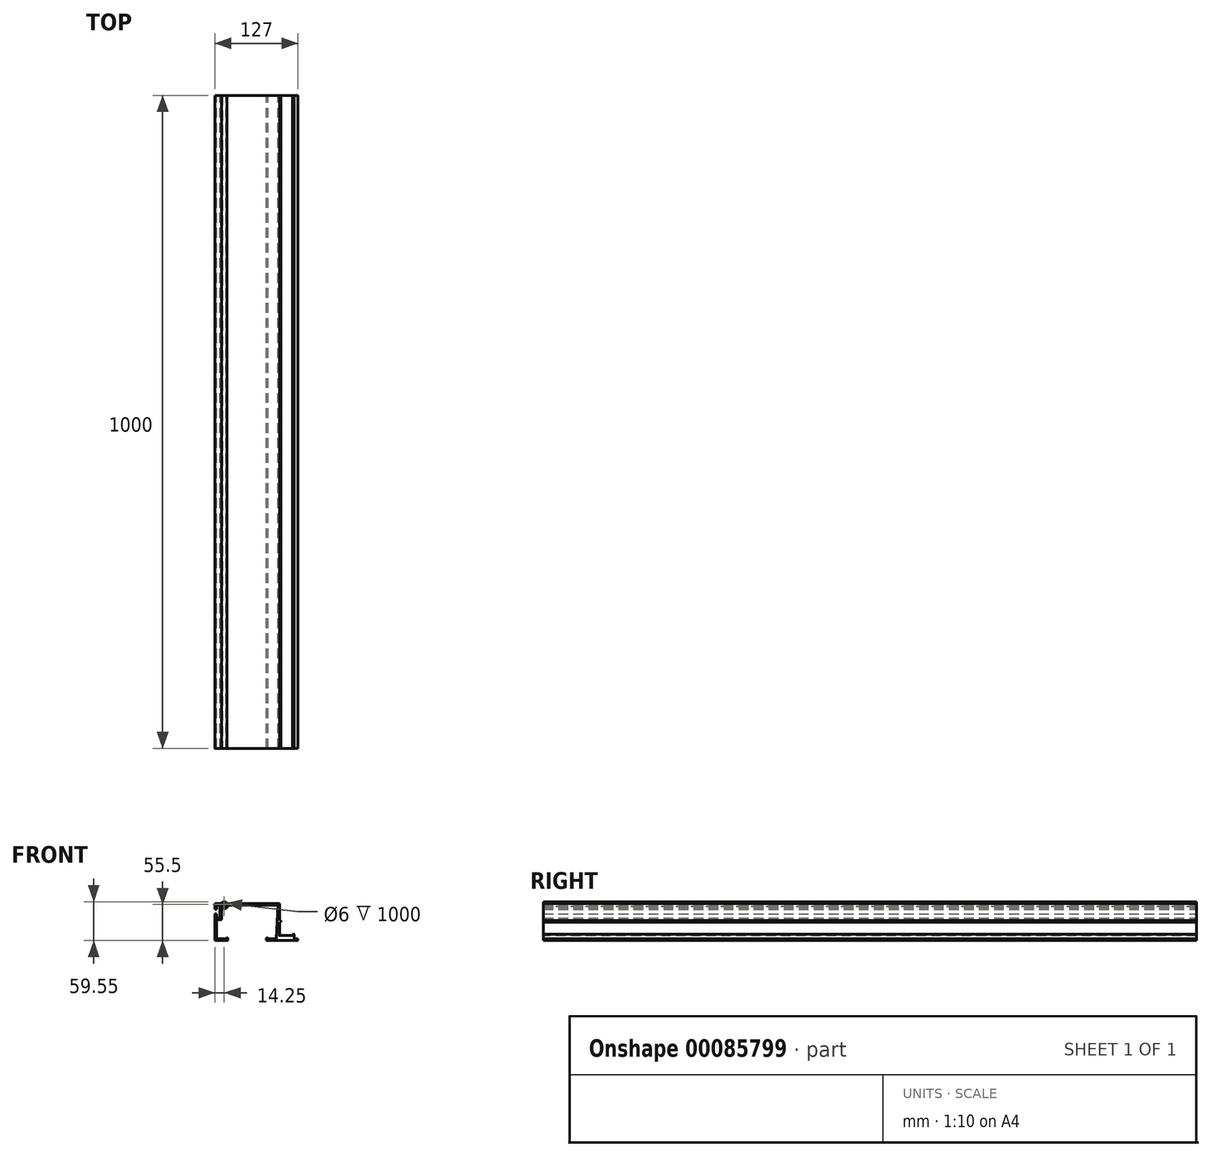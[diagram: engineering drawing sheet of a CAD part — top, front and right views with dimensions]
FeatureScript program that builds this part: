
annotation { "Feature Type Name" : "Feature", "Feature Type Description" : "" }
export const myFeature = defineFeature(function(context is Context, id is Id, definition is map)
    precondition{}
    {
        {
            var Q0;
            Q0=qCreatedBy(makeId("Front.planeOp"),FACE);
            var sketch = newSketch(context, id + "F0", { "sketchPlane" : qUnion([Q0])});
            skLineSegment(sketch, "E0", {"start": v(-113.99, 57) * mm, "end": v(-33, 57) * mm});
            skLineSegment(sketch, "E1", {"start": v(-33, 57) * mm, "end": v(-33, 8) * mm});
            skLineSegment(sketch, "E2", {"start": v(-33, 8) * mm, "end": v(-10.5, 8) * mm});
            skLineSegment(sketch, "E3", {"start": v(-5, 0) * mm, "end": v(-53, 0) * mm});
            skLineSegment(sketch, "E4", {"start": v(-35.5, 54.5) * mm, "end": v(-111.28, 54.5) * mm});
            skLineSegment(sketch, "E5", {"start": v(-132, 0) * mm, "end": v(-112, 0) * mm});
            skLineSegment(sketch, "E6", {"start": v(-112, 0) * mm, "end": v(-112, 4) * mm});
            skLineSegment(sketch, "E7", {"start": v(-35.5, 54.5) * mm, "end": v(-38.23, 2.5) * mm});
            skLineSegment(sketch, "E8", {"start": v(-53, 4) * mm, "end": v(-50.5, 4) * mm});
            skLineSegment(sketch, "E9", {"start": v(-53, 0) * mm, "end": v(-53, 4) * mm});
            skLineSegment(sketch, "E10", {"start": v(-132, 0) * mm, "end": v(-132, 41) * mm});
            skLineSegment(sketch, "E11", {"start": v(-132, 41) * mm, "end": v(-129.5, 41) * mm});
            skLineSegment(sketch, "E12", {"start": v(-129.5, 41) * mm, "end": v(-129.5, 34.5) * mm});
            skLineSegment(sketch, "E13", {"start": v(-129.5, 34.5) * mm, "end": v(-124.3, 34.5) * mm});
            skLineSegment(sketch, "E14", {"start": v(-124.3, 34.5) * mm, "end": v(-124.3, 54.5) * mm});
            skLineSegment(sketch, "E15", {"start": v(-124.3, 54.5) * mm, "end": v(-129.5, 54.5) * mm});
            skLineSegment(sketch, "E16", {"start": v(-129.5, 54.5) * mm, "end": v(-129.5, 48) * mm});
            skLineSegment(sketch, "E17", {"start": v(-129.5, 48) * mm, "end": v(-132, 48) * mm});
            skLineSegment(sketch, "E18", {"start": v(-132, 48) * mm, "end": v(-132, 57) * mm});
            skLineSegment(sketch, "E19", {"start": v(-132, 57) * mm, "end": v(-121.51, 57) * mm});
            skLineSegment(sketch, "E20.0", {"start": v(-121.8, 32) * mm, "end": v(-121.8, 50.35) * mm});
            skLineSegment(sketch, "E21", {"start": v(-129.5, 32) * mm, "end": v(-129.5, 2.5) * mm});
            skLineSegment(sketch, "E22", {"start": v(-129.5, 2.5) * mm, "end": v(-114.5, 2.5) * mm});
            skLineSegment(sketch, "E23", {"start": v(-114.5, 2.5) * mm, "end": v(-114.5, 4) * mm});
            skLineSegment(sketch, "E24", {"start": v(-114.5, 4) * mm, "end": v(-112, 4) * mm});
            skArc(sketch, "E25", {"start": v(-121.8, 50.35) * mm, "mid": v(-115.35, 49.4) * mm, "end": v(-111.28, 54.5) * mm});
            skArc(sketch, "E26", {"start": v(-121.51, 57) * mm, "mid": v(-117.75, 51.45) * mm, "end": v(-113.99, 57) * mm});
            skLineSegment(sketch, "E27", {"start": v(-129.5, 32) * mm, "end": v(-121.8, 32) * mm});
            skLineSegment(sketch, "E28", {"start": v(-50.5, 4) * mm, "end": v(-50.5, 2.5) * mm});
            skLineSegment(sketch, "E29", {"start": v(-50.5, 2.5) * mm, "end": v(-38.23, 2.5) * mm});
            skLineSegment(sketch, "E30", {"start": v(-10.5, 8) * mm, "end": v(-10.5, 2.5) * mm});
            skLineSegment(sketch, "E31", {"start": v(-10.5, 2.5) * mm, "end": v(-5, 2.5) * mm});
            skLineSegment(sketch, "E32", {"start": v(-5, 2.5) * mm, "end": v(-5, 0) * mm});
            skSolve(sketch);
        }
        {
            var Q0;
            Q0=makeQuery(id+"F0.imprint","IMPRINT",FACE,{"disambiguationData":[TD([[makeQuery(id+"F0.imprint","IMPRINT",EDGE,{"derivedFrom":sQuery(id+"F0.wireOp",EDGE,"E0")}),-1.0]])]});
            extrude(context, id + "F1", {"entities" : qUnion([Q0]), "depth" : 1000 * mm});
        }
        {
            var Q0;
            Q0=makeQuery(id+"F1.opExtrude","SWEPT_EDGE",EDGE,{"disambiguationData":[OSD([sQuery(id+"F0.wireOp",EDGE,"E18"),sQuery(id+"F0.wireOp",EDGE,"E19")])]});
            var Q1;
            Q1=makeQuery(id+"F1.opExtrude","SWEPT_EDGE",EDGE,{"disambiguationData":[OSD([sQuery(id+"F0.wireOp",EDGE,"E10"),sQuery(id+"F0.wireOp",EDGE,"E11")])]});
            var Q2;
            Q2=makeQuery(id+"F1.opExtrude","SWEPT_EDGE",EDGE,{"disambiguationData":[OSD([sQuery(id+"F0.wireOp",EDGE,"E5"),sQuery(id+"F0.wireOp",EDGE,"E6")])]});
            var Q3;
            Q3=makeQuery(id+"F1.opExtrude","SWEPT_EDGE",EDGE,{"disambiguationData":[OSD([sQuery(id+"F0.wireOp",EDGE,"E0"),sQuery(id+"F0.wireOp",EDGE,"E1")])]});
            var Q4;
            Q4=makeQuery(id+"F1.opExtrude","SWEPT_EDGE",EDGE,{"disambiguationData":[OSD([sQuery(id+"F0.wireOp",EDGE,"E19"),sQuery(id+"F0.wireOp",EDGE,"E26")])]});
            var Q5;
            Q5=makeQuery(id+"F1.opExtrude","SWEPT_EDGE",EDGE,{"disambiguationData":[OSD([sQuery(id+"F0.wireOp",EDGE,"E0"),sQuery(id+"F0.wireOp",EDGE,"E26")])]});
            var Q6;
            Q6=makeQuery(id+"F1.opExtrude","SWEPT_EDGE",EDGE,{"disambiguationData":[OSD([sQuery(id+"F0.wireOp",EDGE,"E17"),sQuery(id+"F0.wireOp",EDGE,"E18")])]});
            var Q7;
            Q7=makeQuery(id+"F1.opExtrude","SWEPT_EDGE",EDGE,{"disambiguationData":[OSD([sQuery(id+"F0.wireOp",EDGE,"E23"),sQuery(id+"F0.wireOp",EDGE,"E24")])]});
            var Q8;
            Q8=makeQuery(id+"F1.opExtrude","SWEPT_EDGE",EDGE,{"disambiguationData":[OSD([sQuery(id+"F0.wireOp",EDGE,"E6"),sQuery(id+"F0.wireOp",EDGE,"E24")])]});
            var Q9;
            Q9=makeQuery(id+"F1.opExtrude","SWEPT_EDGE",EDGE,{"disambiguationData":[OSD([sQuery(id+"F0.wireOp",EDGE,"E8"),sQuery(id+"F0.wireOp",EDGE,"E9")])]});
            var Q10;
            Q10=makeQuery(id+"F1.opExtrude","SWEPT_EDGE",EDGE,{"disambiguationData":[OSD([sQuery(id+"F0.wireOp",EDGE,"E8"),sQuery(id+"F0.wireOp",EDGE,"E28")])]});
            var Q11;
            Q11=makeQuery(id+"F1.opExtrude","SWEPT_EDGE",EDGE,{"disambiguationData":[OSD([sQuery(id+"F0.wireOp",EDGE,"E3"),sQuery(id+"F0.wireOp",EDGE,"E9")])]});
            var Q12;
            Q12=makeQuery(id+"F1.opExtrude","SWEPT_EDGE",EDGE,{"disambiguationData":[OSD([sQuery(id+"F0.wireOp",EDGE,"E5"),sQuery(id+"F0.wireOp",EDGE,"E10")])]});
            var Q13;
            Q13=makeQuery(id+"F1.opExtrude","SWEPT_EDGE",EDGE,{"disambiguationData":[OSD([sQuery(id+"F0.wireOp",EDGE,"mQSidlCQ-H5td-Nqdc-Uo1I-JofjD6rjHsxK"),sQuery(id+"F0.wireOp",EDGE,"HrKZPL8b-TBKt-fA9s-92uf-cW7PSIgds35S")])]});
            var Q14;
            Q14=makeQuery(id+"F1.opExtrude","SWEPT_EDGE",EDGE,{"disambiguationData":[OSD([sQuery(id+"F0.wireOp",EDGE,"E20.0"),sQuery(id+"F0.wireOp",EDGE,"E27")])]});
            var Q15;
            Q15=makeQuery(id+"F1.opExtrude","SWEPT_EDGE",EDGE,{"disambiguationData":[OSD([sQuery(id+"F0.wireOp",EDGE,"E7"),sQuery(id+"F0.wireOp",EDGE,"E29")])]});
            var Q16;
            Q16=makeQuery(id+"F1.opExtrude","SWEPT_EDGE",EDGE,{"disambiguationData":[OSD([sQuery(id+"F0.wireOp",EDGE,"E4"),sQuery(id+"F0.wireOp",EDGE,"E7")])]});
            var Q17;
            Q17=makeQuery(id+"F1.opExtrude","SWEPT_EDGE",EDGE,{"disambiguationData":[OSD([sQuery(id+"F0.wireOp",EDGE,"E4"),sQuery(id+"F0.wireOp",EDGE,"E25")])]});
            var Q18;
            Q18=makeQuery(id+"F1.opExtrude","SWEPT_EDGE",EDGE,{"disambiguationData":[OSD([sQuery(id+"F0.wireOp",EDGE,"E20.0"),sQuery(id+"F0.wireOp",EDGE,"E25")])]});
            var Q19;
            Q19=makeQuery(id+"F1.opExtrude","SWEPT_EDGE",EDGE,{"disambiguationData":[OSD([sQuery(id+"F0.wireOp",EDGE,"HrKZPL8b-TBKt-fA9s-92uf-cW7PSIgds35S"),sQuery(id+"F0.wireOp",EDGE,"E3")])]});
            fillet(context, id + "F2", {"entities" : qUnion([Q0, Q1, Q2, Q3, Q4, Q5, Q6, Q7, Q8, Q9, Q10, Q11, Q12, Q13, Q14, Q15, Q16, Q17, Q18, Q19]), "radius" : 0.5 * mm, "tangentPropagation" : true, "allowEdgeOverflow" : false});
        }
        {
            var Q0;
            Q0=makeQuery(id+"F1.opExtrude","CAP_FACE",FACE,{"disambiguationData":[OSD([sQuery(id+"F0.wireOp",EDGE,"E0"),sQuery(id+"F0.wireOp",EDGE,"E1"),sQuery(id+"F0.wireOp",EDGE,"E2"),sQuery(id+"F0.wireOp",EDGE,"Jkrs3TaI-eq3d-w76h-wYej-C007znSVGsnd"),sQuery(id+"F0.wireOp",EDGE,"mQSidlCQ-H5td-Nqdc-Uo1I-JofjD6rjHsxK"),sQuery(id+"F0.wireOp",EDGE,"HrKZPL8b-TBKt-fA9s-92uf-cW7PSIgds35S"),sQuery(id+"F0.wireOp",EDGE,"E3"),sQuery(id+"F0.wireOp",EDGE,"E4"),sQuery(id+"F0.wireOp",EDGE,"E5"),sQuery(id+"F0.wireOp",EDGE,"E6"),sQuery(id+"F0.wireOp",EDGE,"E7"),sQuery(id+"F0.wireOp",EDGE,"E8"),sQuery(id+"F0.wireOp",EDGE,"E9"),sQuery(id+"F0.wireOp",EDGE,"E10"),sQuery(id+"F0.wireOp",EDGE,"E11"),sQuery(id+"F0.wireOp",EDGE,"E12"),sQuery(id+"F0.wireOp",EDGE,"E13"),sQuery(id+"F0.wireOp",EDGE,"E14"),sQuery(id+"F0.wireOp",EDGE,"E15"),sQuery(id+"F0.wireOp",EDGE,"E16"),sQuery(id+"F0.wireOp",EDGE,"E17"),sQuery(id+"F0.wireOp",EDGE,"E18"),sQuery(id+"F0.wireOp",EDGE,"E19"),sQuery(id+"F0.wireOp",EDGE,"E20.0"),sQuery(id+"F0.wireOp",EDGE,"E21"),sQuery(id+"F0.wireOp",EDGE,"E22"),sQuery(id+"F0.wireOp",EDGE,"E23"),sQuery(id+"F0.wireOp",EDGE,"E24"),sQuery(id+"F0.wireOp",EDGE,"E25"),sQuery(id+"F0.wireOp",EDGE,"E26"),sQuery(id+"F0.wireOp",EDGE,"E27"),sQuery(id+"F0.wireOp",EDGE,"E28"),sQuery(id+"F0.wireOp",EDGE,"E29")])],"isStart":false});
            var sketch = newSketch(context, id + "F3", { "sketchPlane" : qUnion([Q0])});
            skCircle(sketch, "E33", {"center": v(-33, 8) * mm, "radius": 0.5 * mm});
            skSolve(sketch);
        }
        {
            var Q0;
            {var subQ0=sQuery(id+"F3.wireOp",EDGE,"E33");var subQ1=makeQuery(id+"F1.opExtrude","CAP_EDGE",EDGE,{"disambiguationData":[OSD([sQuery(id+"F0.wireOp",EDGE,"E2")])],"isStart":false});var subQ2=makeQuery(id+"F3.imprint","INTERSECT",VERTEX,{"derivedFrom":[subQ1,subQ0]});Q0=makeQuery(id+"F3.imprint","IMPRINT",FACE,{"disambiguationData":[TD([[makeQuery(id+"F3.imprint","IMPRINT",EDGE,{"disambiguationData":[TD([[subQ2,1.0]])],"derivedFrom":subQ0}),1.0]])]});}
            extrude(context, id + "F4", {"entities" : qUnion([Q0]), "operationType" : NewBodyOperationType.REMOVE, "oppositeDirection" : true, "depth" : 1000 * mm});
        }
        {
            var Q0;
            Q0=makeQuery(id+"F1.opExtrude","CAP_FACE",FACE,{"disambiguationData":[OSD([sQuery(id+"F0.wireOp",EDGE,"E0"),sQuery(id+"F0.wireOp",EDGE,"E1"),sQuery(id+"F0.wireOp",EDGE,"E2"),sQuery(id+"F0.wireOp",EDGE,"Jkrs3TaI-eq3d-w76h-wYej-C007znSVGsnd"),sQuery(id+"F0.wireOp",EDGE,"mQSidlCQ-H5td-Nqdc-Uo1I-JofjD6rjHsxK"),sQuery(id+"F0.wireOp",EDGE,"HrKZPL8b-TBKt-fA9s-92uf-cW7PSIgds35S"),sQuery(id+"F0.wireOp",EDGE,"E3"),sQuery(id+"F0.wireOp",EDGE,"E4"),sQuery(id+"F0.wireOp",EDGE,"E5"),sQuery(id+"F0.wireOp",EDGE,"E6"),sQuery(id+"F0.wireOp",EDGE,"E7"),sQuery(id+"F0.wireOp",EDGE,"E8"),sQuery(id+"F0.wireOp",EDGE,"E9"),sQuery(id+"F0.wireOp",EDGE,"E10"),sQuery(id+"F0.wireOp",EDGE,"E11"),sQuery(id+"F0.wireOp",EDGE,"E12"),sQuery(id+"F0.wireOp",EDGE,"E13"),sQuery(id+"F0.wireOp",EDGE,"E14"),sQuery(id+"F0.wireOp",EDGE,"E15"),sQuery(id+"F0.wireOp",EDGE,"E16"),sQuery(id+"F0.wireOp",EDGE,"E17"),sQuery(id+"F0.wireOp",EDGE,"E18"),sQuery(id+"F0.wireOp",EDGE,"E19"),sQuery(id+"F0.wireOp",EDGE,"E20.0"),sQuery(id+"F0.wireOp",EDGE,"E21"),sQuery(id+"F0.wireOp",EDGE,"E22"),sQuery(id+"F0.wireOp",EDGE,"E23"),sQuery(id+"F0.wireOp",EDGE,"E24"),sQuery(id+"F0.wireOp",EDGE,"E25"),sQuery(id+"F0.wireOp",EDGE,"E26"),sQuery(id+"F0.wireOp",EDGE,"E27"),sQuery(id+"F0.wireOp",EDGE,"E28"),sQuery(id+"F0.wireOp",EDGE,"E29")])],"isStart":false});
            var sketch = newSketch(context, id + "F5", { "sketchPlane" : qUnion([Q0])});
            skLineSegment(sketch, "E34.bottom", {"start": v(-33, 28.1) * mm, "end": v(-31, 28.1) * mm});
            skLineSegment(sketch, "E34.top", {"start": v(-33, 30.6) * mm, "end": v(-31, 30.6) * mm});
            skLineSegment(sketch, "E34.left", {"start": v(-33, 30.6) * mm, "end": v(-33, 28.1) * mm});
            skLineSegment(sketch, "E34.right", {"start": v(-31, 30.6) * mm, "end": v(-31, 28.1) * mm});
            skLineSegment(sketch, "E35.bottom", {"start": v(-10.5, 8) * mm, "end": v(-12.9, 8) * mm});
            skLineSegment(sketch, "E35.top", {"start": v(-10.5, 10) * mm, "end": v(-12.9, 10) * mm});
            skLineSegment(sketch, "E35.left", {"start": v(-10.5, 8) * mm, "end": v(-10.5, 10) * mm});
            skLineSegment(sketch, "E35.right", {"start": v(-12.9, 8) * mm, "end": v(-12.9, 10) * mm});
            skSolve(sketch);
        }
        {
            var Q0;
            Q0=makeQuery(id+"F5.imprint","IMPRINT",FACE,{"disambiguationData":[TD([[makeQuery(id+"F5.imprint","IMPRINT",EDGE,{"derivedFrom":sQuery(id+"F5.wireOp",EDGE,"E34.bottom")}),1.0]])]});
            var Q1;
            Q1=makeQuery(id+"F5.imprint","IMPRINT",FACE,{"disambiguationData":[TD([[makeQuery(id+"F5.imprint","IMPRINT",EDGE,{"derivedFrom":sQuery(id+"F5.wireOp",EDGE,"E35.bottom")}),1.0]])]});
            extrude(context, id + "F6", {"entities" : qUnion([Q0, Q1]), "operationType" : NewBodyOperationType.ADD, "oppositeDirection" : true, "depth" : 1000 * mm});
        }
        {
            var Q0;
            Q0=makeQuery(id+"F6.opExtrude","SWEPT_EDGE",EDGE,{"disambiguationData":[OSD([sQuery(id+"F5.wireOp",EDGE,"E34.top"),sQuery(id+"F5.wireOp",EDGE,"E34.right")])]});
            var Q1;
            Q1=makeQuery(id+"F6.opExtrude","SWEPT_EDGE",EDGE,{"disambiguationData":[OSD([sQuery(id+"F5.wireOp",EDGE,"E35.top"),sQuery(id+"F5.wireOp",EDGE,"E35.left")])]});
            var Q2;
            Q2=makeQuery(id+"F1.opExtrude","SWEPT_EDGE",EDGE,{"disambiguationData":[OSD([sQuery(id+"F0.wireOp",EDGE,"E30"),sQuery(id+"F0.wireOp",EDGE,"E31")])]});
            var Q3;
            Q3=makeQuery(id+"F1.opExtrude","SWEPT_EDGE",EDGE,{"disambiguationData":[OSD([sQuery(id+"F0.wireOp",EDGE,"E31"),sQuery(id+"F0.wireOp",EDGE,"E32")])]});
            fillet(context, id + "F7", {"entities" : qUnion([Q0, Q1, Q2, Q3]), "radius" : 0.5 * mm, "tangentPropagation" : true, "allowEdgeOverflow" : false});
        }
        {
            var Q0;
            Q0=makeQuery(id+"F6.boolean.opBoolean","MERGE",FACE,{"derivedFrom":[makeQuery(id+"F1.opExtrude","CAP_FACE",FACE,{"disambiguationData":[OSD([sQuery(id+"F0.wireOp",EDGE,"E0"),sQuery(id+"F0.wireOp",EDGE,"E1"),sQuery(id+"F0.wireOp",EDGE,"E2"),sQuery(id+"F0.wireOp",EDGE,"E3"),sQuery(id+"F0.wireOp",EDGE,"E4"),sQuery(id+"F0.wireOp",EDGE,"E5"),sQuery(id+"F0.wireOp",EDGE,"E6"),sQuery(id+"F0.wireOp",EDGE,"E7"),sQuery(id+"F0.wireOp",EDGE,"E8"),sQuery(id+"F0.wireOp",EDGE,"E9"),sQuery(id+"F0.wireOp",EDGE,"E10"),sQuery(id+"F0.wireOp",EDGE,"E11"),sQuery(id+"F0.wireOp",EDGE,"E12"),sQuery(id+"F0.wireOp",EDGE,"E13"),sQuery(id+"F0.wireOp",EDGE,"E14"),sQuery(id+"F0.wireOp",EDGE,"E15"),sQuery(id+"F0.wireOp",EDGE,"E16"),sQuery(id+"F0.wireOp",EDGE,"E17"),sQuery(id+"F0.wireOp",EDGE,"E18"),sQuery(id+"F0.wireOp",EDGE,"E19"),sQuery(id+"F0.wireOp",EDGE,"E20.0"),sQuery(id+"F0.wireOp",EDGE,"E21"),sQuery(id+"F0.wireOp",EDGE,"E22"),sQuery(id+"F0.wireOp",EDGE,"E23"),sQuery(id+"F0.wireOp",EDGE,"E24"),sQuery(id+"F0.wireOp",EDGE,"E25"),sQuery(id+"F0.wireOp",EDGE,"E26"),sQuery(id+"F0.wireOp",EDGE,"E27"),sQuery(id+"F0.wireOp",EDGE,"E28"),sQuery(id+"F0.wireOp",EDGE,"E29"),sQuery(id+"F0.wireOp",EDGE,"E30"),sQuery(id+"F0.wireOp",EDGE,"E31"),sQuery(id+"F0.wireOp",EDGE,"E32")])],"isStart":false}),makeQuery(id+"F6.opExtrude","CAP_FACE",FACE,{"disambiguationData":[OSD([sQuery(id+"F5.wireOp",EDGE,"E34.bottom"),sQuery(id+"F5.wireOp",EDGE,"E34.top"),sQuery(id+"F5.wireOp",EDGE,"E34.left"),sQuery(id+"F5.wireOp",EDGE,"E34.right")])],"isStart":true}),makeQuery(id+"F6.opExtrude","CAP_FACE",FACE,{"disambiguationData":[OSD([sQuery(id+"F5.wireOp",EDGE,"E35.bottom"),sQuery(id+"F5.wireOp",EDGE,"E35.top"),sQuery(id+"F5.wireOp",EDGE,"E35.left"),sQuery(id+"F5.wireOp",EDGE,"E35.right")])],"isStart":true})]});
            var sketch = newSketch(context, id + "F8", { "sketchPlane" : qUnion([Q0])});
            skCircle(sketch, "E36", {"center": v(-117.75, 55.5) * mm, "radius": 4.05 * mm});
            skPoint(sketch, "E36.first.point", {"position": v(-121.67, 54.5) * mm});
            skPoint(sketch, "E36.second.point", {"position": v(-117.75, 51.45) * mm});
            skPoint(sketch, "E36.third.point", {"position": v(-113.83, 54.5) * mm});
            skCircle(sketch, "E37.0", {"center": v(-117.75, 55.5) * mm, "radius": 3 * mm});
            skSolve(sketch);
        }
        {
            var Q0;
            Q0=makeQuery(id+"F8.imprint","IMPRINT",FACE,{"disambiguationData":[TD([[makeQuery(id+"F8.imprint","IMPRINT",EDGE,{"derivedFrom":sQuery(id+"F8.wireOp",EDGE,"E37.0")}),-1.0]])]});
            extrude(context, id + "F9", {"entities" : qUnion([Q0]), "oppositeDirection" : true, "depth" : 1000 * mm});
        }
    });
